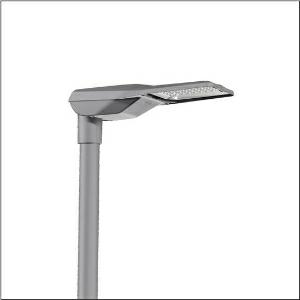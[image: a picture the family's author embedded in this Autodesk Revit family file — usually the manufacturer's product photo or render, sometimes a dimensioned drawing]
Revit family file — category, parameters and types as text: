
# Revit family: streetlight_sl_21_iq_mini___pl52_5xe2h31d08hb_f62b
name_source: partatom
category: Lighting Fixtures
units: mm (PartAtom-declared; Revit-internal decimal feet)

## family parameters
Cut with Voids When Loaded = No
Host = Face
Light Source = No
Part Type = Normal
Room Calculation Point = No
Round Connector Dimension = Use Diameter
Shared = No

## types (1)
- --- (1 x LED, 9290 lm, 70.9 W, 3000K)
    Apparent Load = 71 VA
    CIE Flux Codes = 27 59 98 100 100
    Color Rendering = 70
    Color Temperature = 3000K
    Default Elevation = 1800 mm
    Description = Streetlight SL 21 iQ mini, mast luminaire, primary light control with lens, of PMMA, primary optical cover: cover, of toughened safety glass, transparent, light distribution: PL52, light emission: direct distribution, primary light characteristic: asymmetric, installation type: post-top, side-entry, LED, High Power LED, rated luminous flux: 9.290lm, luminous efficacy: 131lm/W, light colour: 730, colour temperature: 3000K, control gear: iQ-Comfort, control: Auto-Match, Temp-Guard, Lumen-Switch, Night-Set, Smart-Wire, Light-Fading, Desk-Remote (wireless, voltage-free reading and setting of iQ features in the workshop via application-optimized NFC function/RFID function), optimised constant luminous flux control (CLO 2.0), pre-setting: linear dimming characteristic, mains connection: 220..240V, AC, 50/60Hz, start of lifetime: 71W, end of service life: 75W, reduction: 31W, luminaire housing, of diecast aluminium, powder-coated, Siteco® metallic grey (DB 702S), corrosivity category C5 mid according to DIN EN ISO 12944, please order mast flange separately, inclination adjustable: 0°, 5°, 10°, 15°, sealing non-destructively replaceable, multi-level sealing system, length: 628mm, width: 235mm, height: 110mm, mast flange for spigot size: 42mm (side-entry): 5XC10008XM4, 60/48mm (side-entry/post-top): 5XC10108XM2, 76/60mm (side-entry/post-top): 5XC10108XM1, mounting height: 4..8m, protection rating (complete): IP66, insulation class (complete): insulation class II (safety insulation), certification: CE, ENEC, ENEC+, VDE, impact resistance: IK10, permissible operating ambient temperature for outdoor applications: -40..+50°C, standard-compliant lighting for roads and squares, packaging unit: 1 piece

Light Distribution: PL52
    Height = 110 mm
    Lamp = 1 x LED
    Lamp Light Flux = 9290 lm
    Lamp Power = 70.9 W
    Lamp count = 1
    Length = 625 mm
    Luminous efficacy = 131 lm/W
    Manufacturer = Siteco
    ModVariant = No
    Model = 5XE2H31D08HB
    Number of Poles = 1
    OnlyDefault = Yes
    Power Factor = 1
    Product Name = Streetlight SL 21 iQ mini | PL52
    Product group = mast luminaire | pylon top
    ProductGroupID = 6100
    Protection Class = Protection class II
    Protection Degree = IP 66
    RLX_Detail_Level = 1
    RLX_Emergency_Light_Flux = 0 lm
    RLX_Emergency_Type = 0
    RLX_Emergency_Type_DB = No
    RlxData = <blob elided: 35941 chars, md5=77b70160>
    Socket = socket
    Standby Power = 0 W
    System Light Flux = 9290 lm
    System Power = 71 W
    Type Comments = factory setting: luminous flux: 100 % | dim-lin: 254 | 711 mA
    Type Image = l_1003519.jpg
    URL = http://relux.com
    VarID = @adj_158492
    Voltage = 0 V
    Weight = 0.00 kg
    Width = 234 mm

## geometry (parser evidence)
native form markers: Blend x4, Sweep x9
no freeform markers — native parametric forms only
